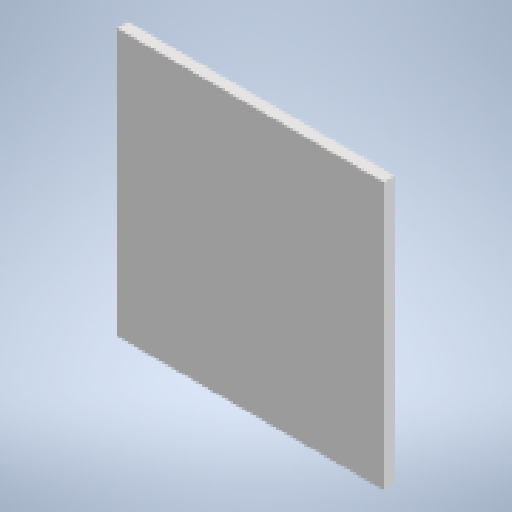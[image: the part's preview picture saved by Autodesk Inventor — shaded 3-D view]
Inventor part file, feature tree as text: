
AUTODESK INVENTOR PART (.ipt)
format: ipt  version: 2023 (Build 270158000, 158)  size: 118,784 bytes
history: native  units: mm
features: extrude x1, sketch x1
ambient origin geometry x8: Origin, YZ Plane, XZ Plane, XY Plane, X Axis, Y Axis, Z Axis, Center Point
bodies: Solid1 (feature_tree)
feature tree (2):
  extrude  "Extrusion1"  Depth=609.6mm
  sketch  "Sketch1"  dims[d0=609.6mm d1=609.6mm d2=25.4mm d3=0.0mm]
